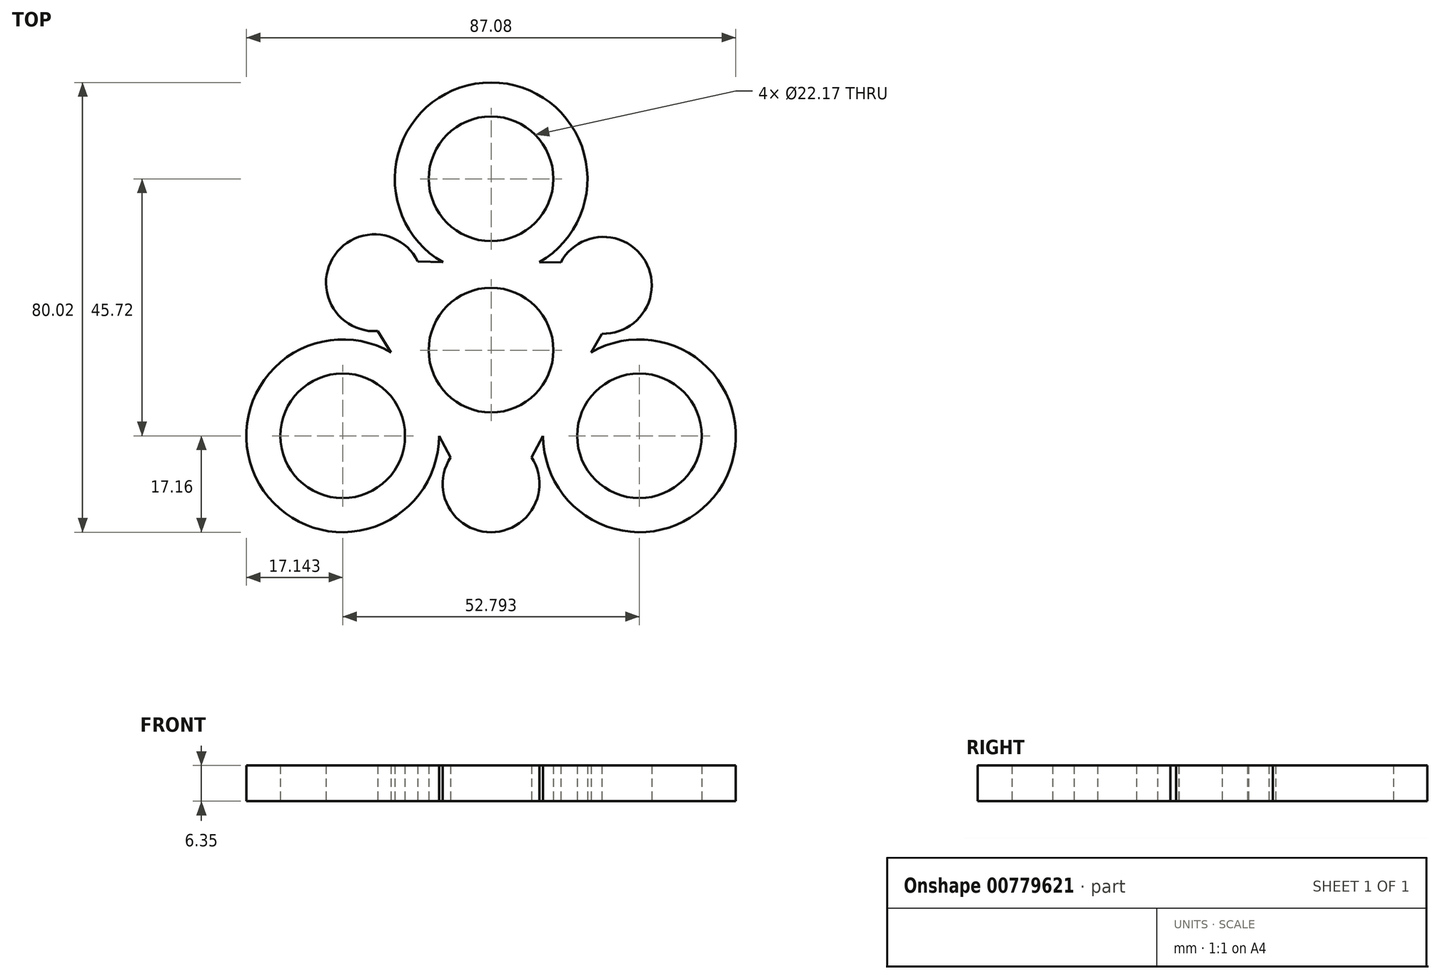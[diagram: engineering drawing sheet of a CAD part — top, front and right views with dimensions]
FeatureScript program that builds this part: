
annotation { "Feature Type Name" : "Feature", "Feature Type Description" : "" }
export const myFeature = defineFeature(function(context is Context, id is Id, definition is map)
    precondition{}
    {
        {
            var Q0;
            Q0=qCreatedBy(makeId("Top.planeOp"),FACE);
            var sketch = newSketch(context, id + "F0", { "sketchPlane" : qUnion([Q0])});
            skCircle(sketch, "E0", {"center": v(0, 0) * mm, "radius": 11.09 * mm});
            skCircle(sketch, "E1", {"center": v(0, 30.48) * mm, "radius": 11.09 * mm});
            skCircle(sketch, "E2", {"center": v(26.4, -15.24) * mm, "radius": 11.09 * mm});
            skCircle(sketch, "E3", {"center": v(-26.4, -15.24) * mm, "radius": 11.09 * mm});
            skCircle(sketch, "E4", {"center": v(-26.4, -15.24) * mm, "radius": 17.15 * mm});
            skCircle(sketch, "E5", {"center": v(26.4, -15.24) * mm, "radius": 17.15 * mm});
            skCircle(sketch, "E6", {"center": v(0, 30.48) * mm, "radius": 17.15 * mm});
            skLineSegment(sketch, "E7", {"start": v(0, -32.33) * mm, "end": v(-9.25, -15.24) * mm});
            skLineSegment(sketch, "E8", {"start": v(0, -32.33) * mm, "end": v(9.25, -15.24) * mm});
            skLineSegment(sketch, "E9", {"start": v(-28.31, 16.35) * mm, "end": v(-8.57, 15.63) * mm});
            skLineSegment(sketch, "E10", {"start": v(-28.31, 16.35) * mm, "end": v(-17.82, -0.4) * mm});
            skLineSegment(sketch, "E11", {"start": v(8.57, 15.63) * mm, "end": v(26.75, 15.44) * mm});
            skLineSegment(sketch, "E12", {"start": v(26.75, 15.44) * mm, "end": v(17.82, -0.4) * mm});
            skCircle(sketch, "E13", {"center": v(-20.76, 11.98) * mm, "radius": 8.61 * mm});
            skCircle(sketch, "E14", {"center": v(19.97, 11.53) * mm, "radius": 8.61 * mm});
            skCircle(sketch, "E15", {"center": v(0, -23.79) * mm, "radius": 8.61 * mm});
            skSolve(sketch);
        }
        {
            var Q0;
            {var subQ0=sQuery(id+"F0.wireOp",EDGE,"E13");var subQ1=sQuery(id+"F0.wireOp",EDGE,"E9");var subQ2=makeQuery(id+"F0.imprint","INTERSECT",VERTEX,{"disambiguationData":[OD(0.0)],"derivedFrom":[subQ1,subQ0]});Q0=makeQuery(id+"F0.imprint","IMPRINT",FACE,{"disambiguationData":[TD([[makeQuery(id+"F0.imprint","IMPRINT",EDGE,{"disambiguationData":[TD([[subQ2,-1.0]])],"derivedFrom":subQ1}),1.0]])]});}
            var Q1;
            {var subQ0=sQuery(id+"F0.wireOp",EDGE,"E13");var subQ1=sQuery(id+"F0.wireOp",EDGE,"E10");var subQ2=makeQuery(id+"F0.imprint","INTERSECT",VERTEX,{"disambiguationData":[OD(0.0)],"derivedFrom":[subQ1,subQ0]});Q1=makeQuery(id+"F0.imprint","IMPRINT",FACE,{"disambiguationData":[TD([[makeQuery(id+"F0.imprint","IMPRINT",EDGE,{"disambiguationData":[TD([[subQ2,-1.0]])],"derivedFrom":subQ1}),-1.0]])]});}
            var Q2;
            {var subQ0=sQuery(id+"F0.wireOp",EDGE,"E13");var subQ1=sQuery(id+"F0.wireOp",EDGE,"E9");var subQ2=makeQuery(id+"F0.imprint","INTERSECT",VERTEX,{"disambiguationData":[OD(0.0)],"derivedFrom":[subQ1,subQ0]});Q2=makeQuery(id+"F0.imprint","IMPRINT",FACE,{"disambiguationData":[TD([[makeQuery(id+"F0.imprint","IMPRINT",EDGE,{"disambiguationData":[TD([[subQ2,-1.0]])],"derivedFrom":subQ1}),-1.0]])]});}
            var Q3;
            Q3=makeQuery(id+"F0.imprint","IMPRINT",FACE,{"disambiguationData":[TD([[makeQuery(id+"F0.imprint","IMPRINT",EDGE,{"derivedFrom":sQuery(id+"F0.wireOp",EDGE,"E0")}),-1.0]])]});
            var Q4;
            Q4=makeQuery(id+"F0.imprint","IMPRINT",FACE,{"disambiguationData":[TD([[makeQuery(id+"F0.imprint","IMPRINT",EDGE,{"derivedFrom":sQuery(id+"F0.wireOp",EDGE,"E1")}),-1.0]])]});
            var Q5;
            {var subQ0=sQuery(id+"F0.wireOp",EDGE,"E12");var subQ1=sQuery(id+"F0.wireOp",EDGE,"E11");var subQ2=makeQuery(id+"F0.imprint","INTERSECT",VERTEX,{"derivedFrom":[subQ1,subQ0]});Q5=makeQuery(id+"F0.imprint","IMPRINT",FACE,{"disambiguationData":[TD([[makeQuery(id+"F0.imprint","IMPRINT",EDGE,{"disambiguationData":[TD([[subQ2,1.0]])],"derivedFrom":subQ1}),-1.0]])]});}
            var Q6;
            {var subQ0=sQuery(id+"F0.wireOp",EDGE,"E12");var subQ1=sQuery(id+"F0.wireOp",EDGE,"E11");var subQ2=makeQuery(id+"F0.imprint","INTERSECT",VERTEX,{"derivedFrom":[subQ1,subQ0]});Q6=makeQuery(id+"F0.imprint","IMPRINT",FACE,{"disambiguationData":[TD([[makeQuery(id+"F0.imprint","IMPRINT",EDGE,{"disambiguationData":[TD([[subQ2,1.0]])],"derivedFrom":subQ1}),1.0]])]});}
            var Q7;
            Q7=makeQuery(id+"F0.imprint","IMPRINT",FACE,{"disambiguationData":[TD([[makeQuery(id+"F0.imprint","IMPRINT",EDGE,{"derivedFrom":sQuery(id+"F0.wireOp",EDGE,"E2")}),-1.0]])]});
            var Q8;
            Q8=makeQuery(id+"F0.imprint","IMPRINT",FACE,{"disambiguationData":[TD([[makeQuery(id+"F0.imprint","IMPRINT",EDGE,{"derivedFrom":sQuery(id+"F0.wireOp",EDGE,"E3")}),-1.0]])]});
            var Q9;
            {var subQ0=sQuery(id+"F0.wireOp",EDGE,"E8");var subQ1=sQuery(id+"F0.wireOp",EDGE,"E7");var subQ2=makeQuery(id+"F0.imprint","INTERSECT",VERTEX,{"derivedFrom":[subQ1,subQ0]});Q9=makeQuery(id+"F0.imprint","IMPRINT",FACE,{"disambiguationData":[TD([[makeQuery(id+"F0.imprint","IMPRINT",EDGE,{"disambiguationData":[TD([[subQ2,-1.0]])],"derivedFrom":subQ1}),-1.0]])]});}
            var Q10;
            {var subQ0=sQuery(id+"F0.wireOp",EDGE,"E8");var subQ1=sQuery(id+"F0.wireOp",EDGE,"E7");var subQ2=makeQuery(id+"F0.imprint","INTERSECT",VERTEX,{"derivedFrom":[subQ1,subQ0]});Q10=makeQuery(id+"F0.imprint","IMPRINT",FACE,{"disambiguationData":[TD([[makeQuery(id+"F0.imprint","IMPRINT",EDGE,{"disambiguationData":[TD([[subQ2,-1.0]])],"derivedFrom":subQ1}),1.0]])]});}
            extrude(context, id + "F1", {"entities" : qUnion([Q0, Q1, Q2, Q3, Q4, Q5, Q6, Q7, Q8, Q9, Q10]), "depth" : 6.35 * mm, "offsetDistance" : 25.4 * mm});
        }
    });
